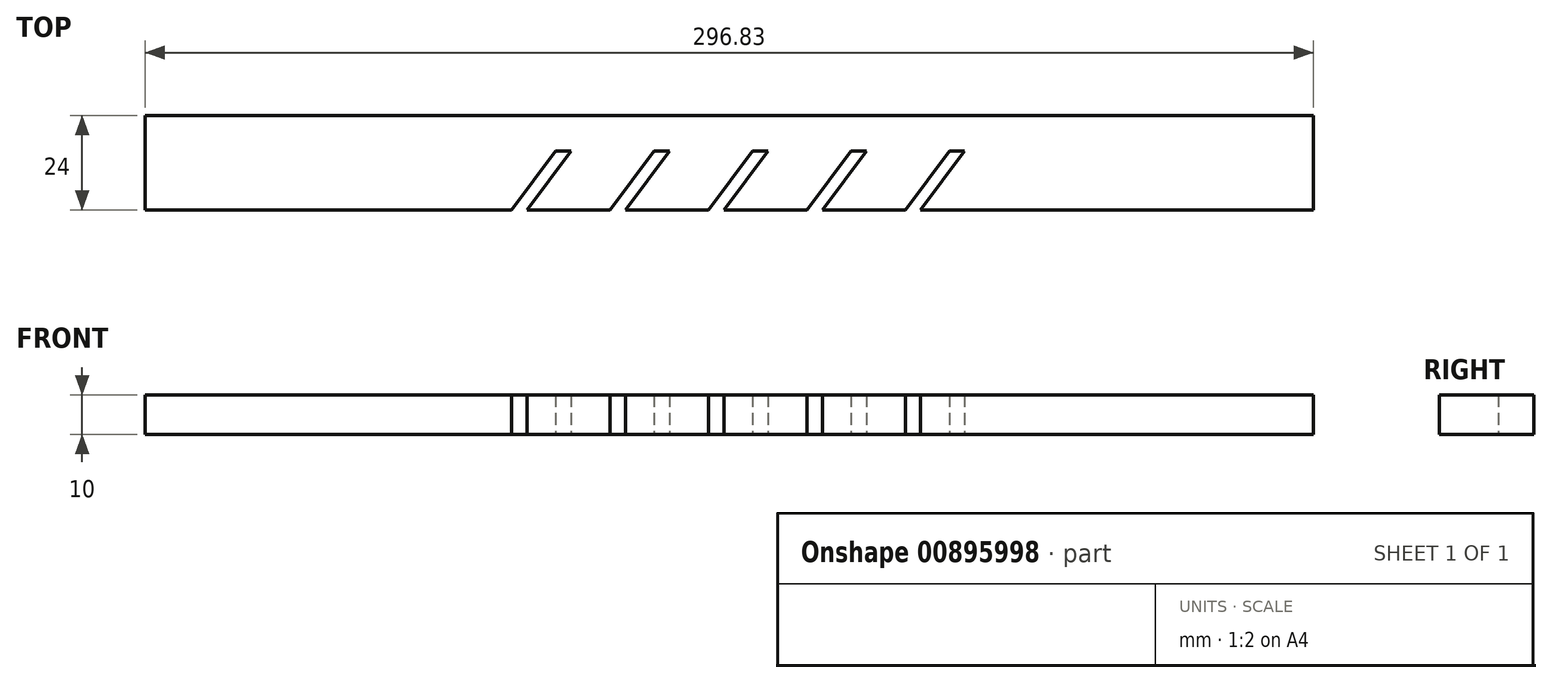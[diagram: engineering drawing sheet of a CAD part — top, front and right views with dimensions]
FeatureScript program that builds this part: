
annotation { "Feature Type Name" : "Feature", "Feature Type Description" : "" }
export const myFeature = defineFeature(function(context is Context, id is Id, definition is map)
    precondition{}
    {
        {
            var Q0;
            Q0=qCreatedBy(makeId("Top.planeOp"),FACE);
            var sketch = newSketch(context, id + "F0", { "sketchPlane" : qUnion([Q0])});
            skLineSegment(sketch, "E0.bottom", {"start": v(-154.43, 12) * mm, "end": v(142.4, 12) * mm});
            skLineSegment(sketch, "E0.top", {"start": v(-154.43, -12) * mm, "end": v(-61.3, -12) * mm});
            skLineSegment(sketch, "E0.left", {"start": v(-154.43, 12) * mm, "end": v(-154.43, -12) * mm});
            skLineSegment(sketch, "E0.right", {"start": v(142.4, 12) * mm, "end": v(142.4, -12) * mm});
            skLineSegment(sketch, "E1", {"start": v(-61.3, -12) * mm, "end": v(-50.13, 3) * mm});
            skLineSegment(sketch, "E2", {"start": v(-50.13, 3) * mm, "end": v(-46.24, 3) * mm});
            skLineSegment(sketch, "E3", {"start": v(-46.24, 3) * mm, "end": v(-57.42, -12) * mm});
            skLineSegment(sketch, "E4.1.0.0", {"start": v(-21.24, 3) * mm, "end": v(-32.42, -12) * mm});
            skLineSegment(sketch, "E4.1.0.1", {"start": v(-25.13, 3) * mm, "end": v(-21.24, 3) * mm});
            skLineSegment(sketch, "E4.1.0.2", {"start": v(-36.3, -12) * mm, "end": v(-25.13, 3) * mm});
            skLineSegment(sketch, "E4.2.0.0", {"start": v(3.76, 3) * mm, "end": v(-7.42, -12) * mm});
            skLineSegment(sketch, "E4.2.0.1", {"start": v(-0.13, 3) * mm, "end": v(3.76, 3) * mm});
            skLineSegment(sketch, "E4.2.0.2", {"start": v(-11.3, -12) * mm, "end": v(-0.13, 3) * mm});
            skLineSegment(sketch, "E4.3.0.0", {"start": v(28.76, 3) * mm, "end": v(17.58, -12) * mm});
            skLineSegment(sketch, "E4.3.0.1", {"start": v(24.87, 3) * mm, "end": v(28.76, 3) * mm});
            skLineSegment(sketch, "E4.3.0.2", {"start": v(13.7, -12) * mm, "end": v(24.87, 3) * mm});
            skLineSegment(sketch, "E4.4.0.0", {"start": v(53.76, 3) * mm, "end": v(42.58, -12) * mm});
            skLineSegment(sketch, "E4.4.0.1", {"start": v(49.87, 3) * mm, "end": v(53.76, 3) * mm});
            skLineSegment(sketch, "E4.4.0.2", {"start": v(38.7, -12) * mm, "end": v(49.87, 3) * mm});
            skLineSegment(sketch, "E4.direction1", {"start": v(-57.42, -12) * mm, "end": v(-36.3, -12) * mm, "construction": true});
            skLineSegment(sketch, "E5.trimOffspring", {"start": v(-57.42, -12) * mm, "end": v(-36.3, -12) * mm});
            skLineSegment(sketch, "E6.trimOffspring", {"start": v(-7.42, -12) * mm, "end": v(13.7, -12) * mm});
            skLineSegment(sketch, "E7.trimOffspring", {"start": v(-32.42, -12) * mm, "end": v(-11.3, -12) * mm});
            skLineSegment(sketch, "E8.trimOffspring", {"start": v(17.58, -12) * mm, "end": v(38.7, -12) * mm});
            skLineSegment(sketch, "E9.trimOffspring", {"start": v(42.58, -12) * mm, "end": v(142.4, -12) * mm});
            skSolve(sketch);
        }
        {
            var Q0;
            Q0=makeQuery(id+"F0.imprint","IMPRINT",FACE,{"disambiguationData":[TD([[makeQuery(id+"F0.imprint","IMPRINT",EDGE,{"derivedFrom":sQuery(id+"F0.wireOp",EDGE,"E0.bottom")}),-1.0]])]});
            extrude(context, id + "F1", {"entities" : qUnion([Q0]), "depth" : 5 * mm, "offsetDistance" : 25 * mm, "hasSecondDirection" : true, "secondDirectionOppositeDirection" : true, "secondDirectionDepth" : 5 * mm});
        }
    });
